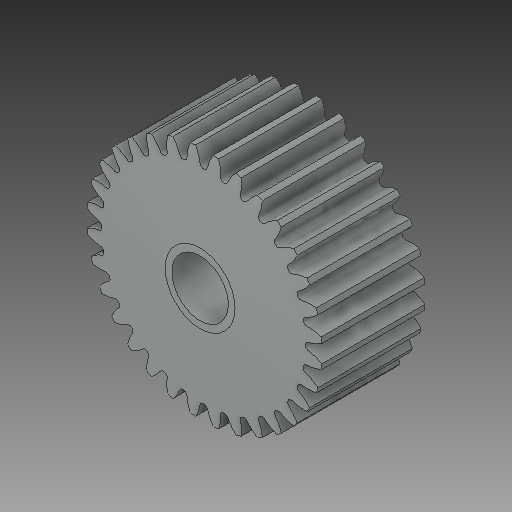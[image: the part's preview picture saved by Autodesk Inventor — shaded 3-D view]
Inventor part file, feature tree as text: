
AUTODESK INVENTOR PART (.ipt)
format: ipt  version: 2017 (Build 210142000, 142)  size: 519,168 bytes
history: native  units: in
note: dims shown in document units (in); Inventor stores cm internally (conversion verified against a paired STEP export)
features: mirror x1
ambient origin geometry x8: Origin, YZ Plane, XZ Plane, XY Plane, X Axis, Y Axis, Z Axis, Center Point
bodies: Solid1 (feature_tree)
feature tree (1):
  mirror  "Mirror1"
